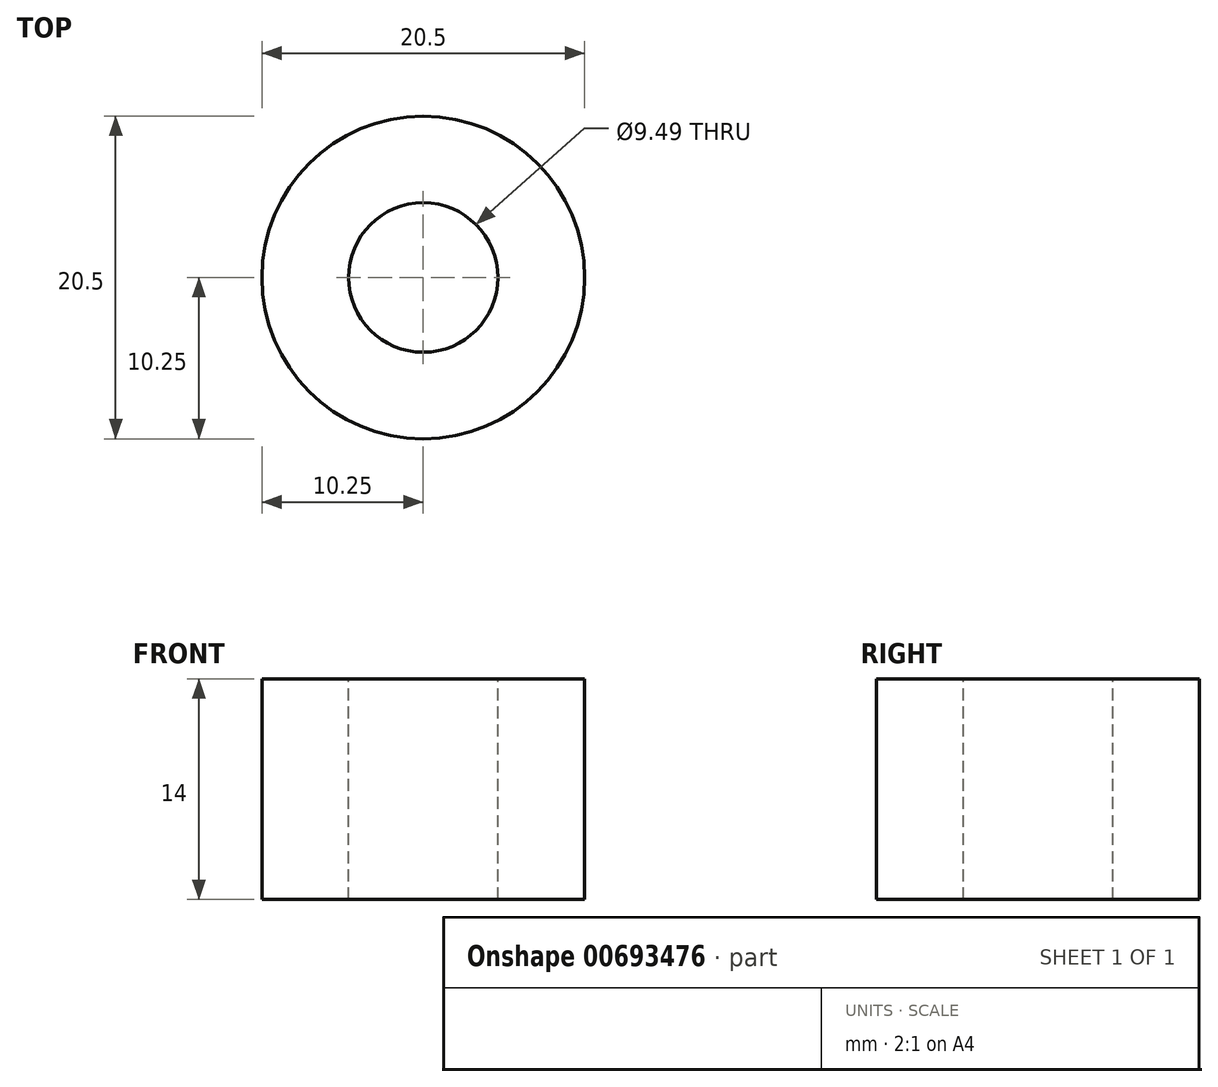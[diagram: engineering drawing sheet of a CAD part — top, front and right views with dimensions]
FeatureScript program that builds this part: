
annotation { "Feature Type Name" : "Feature", "Feature Type Description" : "" }
export const myFeature = defineFeature(function(context is Context, id is Id, definition is map)
    precondition{}
    {
        {
            var Q0;
            Q0=qCreatedBy(makeId("Top.planeOp"),FACE);
            var sketch = newSketch(context, id + "F0", { "sketchPlane" : qUnion([Q0])});
            skCircle(sketch, "E0", {"center": v(0, 0) * mm, "radius": 10.25 * mm});
            skSolve(sketch);
        }
        {
            var Q0;
            Q0=qSketchRegion(id+"F0",true);
            extrude(context, id + "F1", {"entities" : qUnion([Q0]), "depth" : 14 * mm, "offsetDistance" : 25 * mm});
        }
        {
            var Q0;
            Q0=makeQuery(id+"F1.opExtrude","CAP_FACE",FACE,{"disambiguationData":[OSD([sQuery(id+"F0.wireOp",EDGE,"E0")])],"isStart":false});
            var sketch = newSketch(context, id + "F2", { "sketchPlane" : qUnion([Q0])});
            skCircle(sketch, "E1", {"center": v(0, 0) * mm, "radius": 4.75 * mm});
            skSolve(sketch);
        }
        {
            var Q0;
            Q0=makeQuery(id+"F2.imprint","IMPRINT",FACE,{"disambiguationData":[TD([[makeQuery(id+"F2.imprint","IMPRINT",EDGE,{"derivedFrom":sQuery(id+"F2.wireOp",EDGE,"E1")}),1.0]])]});
            extrude(context, id + "F3", {"entities" : qUnion([Q0]), "operationType" : NewBodyOperationType.REMOVE, "depth" : -14 * mm, "offsetDistance" : 25 * mm});
        }
    });
